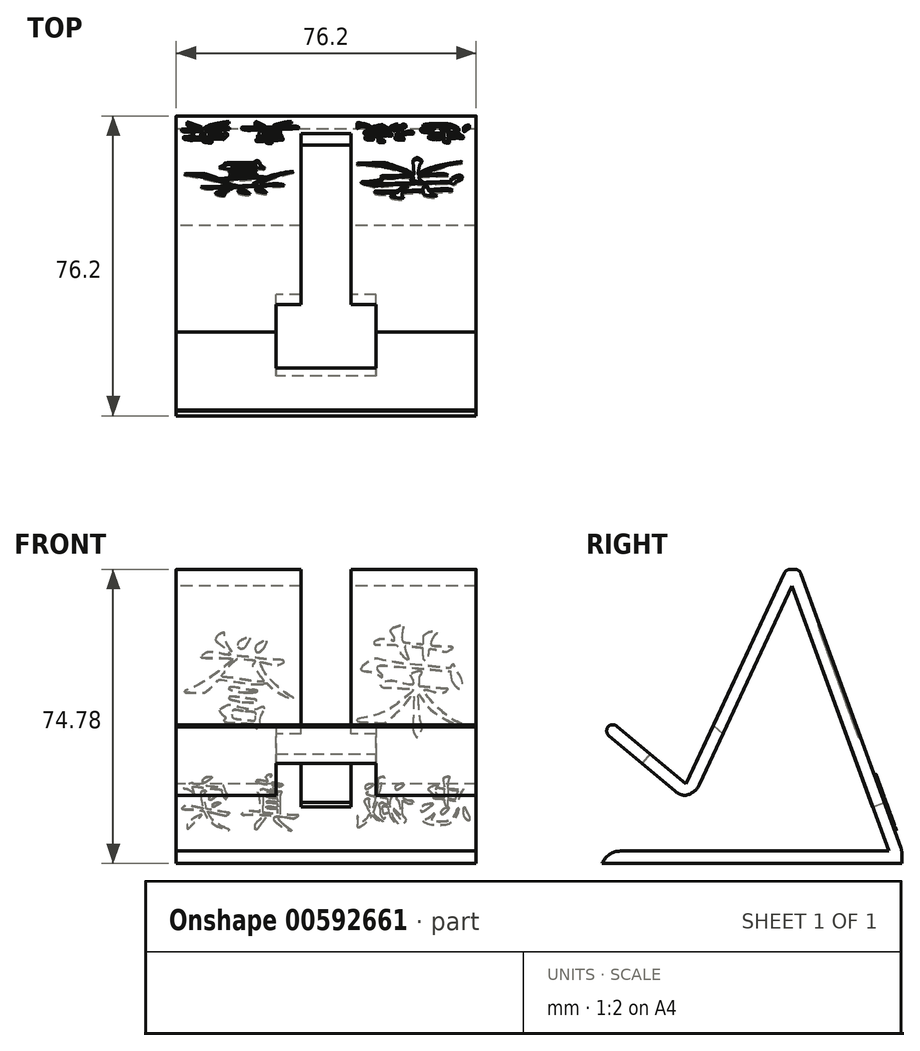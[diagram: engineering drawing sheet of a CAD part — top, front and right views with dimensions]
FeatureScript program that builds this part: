
annotation { "Feature Type Name" : "Feature", "Feature Type Description" : "" }
export const myFeature = defineFeature(function(context is Context, id is Id, definition is map)
    precondition{}
    {
        {
            var Q0;
            Q0=qCreatedBy(makeId("Top.planeOp"),FACE);
            var sketch = newSketch(context, id + "F0", { "sketchPlane" : qUnion([Q0])});
            skLineSegment(sketch, "E0.bottom", {"start": v(-50.93, 28.39) * mm, "end": v(25.27, 28.39) * mm});
            skLineSegment(sketch, "E0.top", {"start": v(-50.93, -47.81) * mm, "end": v(25.27, -47.81) * mm});
            skLineSegment(sketch, "E0.left", {"start": v(-50.93, 28.39) * mm, "end": v(-50.93, -47.81) * mm});
            skLineSegment(sketch, "E0.right", {"start": v(25.27, 28.39) * mm, "end": v(25.27, -47.81) * mm});
            skSolve(sketch);
        }
        {
            var Q0;
            Q0 = qSketchRegion(id + "F0", true);
            extrude(context, id + "F1", {"entities" : qUnion([Q0]), "depth" : 3.17 * mm, "offsetDistance" : 25.4 * mm});
        }
        {
            var Q0;
            Q0=makeQuery(id+"F1.opExtrude","SWEPT_FACE",FACE,{"disambiguationData":[OSD([sQuery(id+"F0.wireOp",EDGE,"E0.left")])]});
            var sketch = newSketch(context, id + "F2", { "sketchPlane" : qUnion([Q0])});
            skLineSegment(sketch, "E1", {"start": v(-28.39, 3.17) * mm, "end": v(-2.33, 74.78) * mm});
            skLineSegment(sketch, "E2", {"start": v(-25, 3.18) * mm, "end": v(1.05, 74.78) * mm});
            skLineSegment(sketch, "E3", {"start": v(1.05, 74.78) * mm, "end": v(-2.33, 74.78) * mm});
            skLineSegment(sketch, "E4", {"start": v(27.89, 17.23) * mm, "end": v(1.05, 74.78) * mm});
            skLineSegment(sketch, "E5", {"start": v(47.35, 33.56) * mm, "end": v(27.89, 17.23) * mm});
            skLineSegment(sketch, "E6", {"start": v(-0.48, 70.56) * mm, "end": v(24.39, 17.23) * mm});
            skLineSegment(sketch, "E7", {"start": v(24.39, 17.23) * mm, "end": v(27.89, 17.23) * mm});
            skLineSegment(sketch, "E8", {"start": v(47.35, 33.56) * mm, "end": v(45.3, 35.99) * mm});
            skLineSegment(sketch, "E9", {"start": v(45.3, 35.99) * mm, "end": v(26.5, 20.2) * mm});
            skSolve(sketch);
        }
        {
            var Q0;
            Q0 = qSketchRegion(id + "F2", true);
            var Q1;
            {var subQ6=sQuery(id+"F2.wireOp",EDGE,"E1");Q1=makeQuery(id+"F2.imprint","IMPRINT",FACE,{"disambiguationData":[TD([[makeQuery(id+"F2.imprint","IMPRINT",EDGE,{"derivedFrom":subQ6}),-1.0]])]});}
            extrude(context, id + "F3", {"entities" : qUnion([Q0, Q1]), "operationType" : NewBodyOperationType.ADD, "oppositeDirection" : true, "depth" : 76.2 * mm, "offsetDistance" : 25.4 * mm});
        }
        {
            var Q0;
            Q0=makeQuery(id+"F3.opExtrude","SWEPT_EDGE",EDGE,{"disambiguationData":[OSD([sQuery(id+"F2.wireOp",EDGE,"E2"),sQuery(id+"F2.wireOp",EDGE,"E3"),sQuery(id+"F2.wireOp",EDGE,"E4")])]});
            var Q1;
            Q1=makeQuery(id+"F3.opExtrude","SWEPT_EDGE",EDGE,{"disambiguationData":[OSD([sQuery(id+"F2.wireOp",EDGE,"E1"),sQuery(id+"F2.wireOp",EDGE,"E3")])]});
            fillet(context, id + "F4", {"entities" : qUnion([Q0, Q1]), "radius" : 1.71 * mm, "tangentPropagation" : true, "allowEdgeOverflow" : false});
        }
        {
            var Q0;
            {var subQ0=sQuery(id+"F0.wireOp",EDGE,"E0.bottom");Q0=makeQuery(id+"F3.boolean.opBoolean","MERGE",EDGE,{"derivedFrom":[makeQuery(id+"F1.opExtrude","CAP_EDGE",EDGE,{"disambiguationData":[OSD([subQ0])],"isStart":false}),makeQuery(id+"F3.opExtrude","SWEPT_EDGE",EDGE,{"disambiguationData":[OSD([subQ0,sQuery(id+"F0.wireOp",EDGE,"E0.left"),sQuery(id+"F2.wireOp",EDGE,"E1")])]})]});}
            fillet(context, id + "F5", {"entities" : qUnion([Q0]), "radius" : 5.08 * mm, "tangentPropagation" : true, "allowEdgeOverflow" : false});
        }
        {
            var Q0;
            Q0=makeQuery(id+"F3.opExtrude","SWEPT_EDGE",EDGE,{"disambiguationData":[OSD([sQuery(id+"F2.wireOp",EDGE,"E8"),sQuery(id+"F2.wireOp",EDGE,"E9")])]});
            var Q1;
            Q1=makeQuery(id+"F3.opExtrude","SWEPT_EDGE",EDGE,{"disambiguationData":[OSD([sQuery(id+"F2.wireOp",EDGE,"E5"),sQuery(id+"F2.wireOp",EDGE,"E8")])]});
            fillet(context, id + "F6", {"entities" : qUnion([Q0, Q1]), "radius" : 1.71 * mm, "tangentPropagation" : true, "allowEdgeOverflow" : false});
        }
        {
            var Q0;
            Q0=makeQuery(id+"F3.opExtrude","SWEPT_EDGE",EDGE,{"disambiguationData":[OSD([sQuery(id+"F2.wireOp",EDGE,"E6"),sQuery(id+"F2.wireOp",EDGE,"E7")])]});
            var Q1;
            Q1=makeQuery(id+"F3.opExtrude","SWEPT_EDGE",EDGE,{"disambiguationData":[OSD([sQuery(id+"F2.wireOp",EDGE,"E4"),sQuery(id+"F2.wireOp",EDGE,"E5"),sQuery(id+"F2.wireOp",EDGE,"E7")])]});
            fillet(context, id + "F7", {"entities" : qUnion([Q0, Q1]), "radius" : 5.08 * mm, "tangentPropagation" : true, "allowEdgeOverflow" : false});
        }
        {
            var Q0;
            Q0=makeQuery(id+"F1.opExtrude","CAP_EDGE",EDGE,{"disambiguationData":[OSD([sQuery(id+"F0.wireOp",EDGE,"E0.top")])],"isStart":false});
            fillet(context, id + "F8", {"entities" : qUnion([Q0]), "radius" : 5.08 * mm, "tangentPropagation" : true, "allowEdgeOverflow" : false});
        }
        {
            var Q0;
            Q0=makeQuery(id+"F3.opExtrude","SWEPT_FACE",FACE,{"disambiguationData":[OSD([sQuery(id+"F2.wireOp",EDGE,"E1")])]});
            var sketch = newSketch(context, id + "F9", { "sketchPlane" : qUnion([Q0])});
            skLineSegment(sketch, "E10.bottom", {"start": v(6.48, 6.38) * mm, "end": v(19.18, 6.38) * mm});
            skLineSegment(sketch, "E10.top", {"start": v(6.48, 82.58) * mm, "end": v(19.18, 82.58) * mm});
            skLineSegment(sketch, "E10.left", {"start": v(6.48, 6.38) * mm, "end": v(6.48, 82.58) * mm});
            skLineSegment(sketch, "E10.right", {"start": v(19.18, 6.38) * mm, "end": v(19.18, 82.58) * mm});
            skSolve(sketch);
        }
        {
            var Q0;
            Q0 = qSketchRegion(id + "F9", true);
            var Q1;
            Q1=makeQuery(id+"F3.opExtrude","SWEPT_FACE",FACE,{"disambiguationData":[OSD([sQuery(id+"F2.wireOp",EDGE,"E9")])]});
            extrude(context, id + "F10", {"entities" : qUnion([Q0]), "operationType" : NewBodyOperationType.REMOVE, "endBound" : BoundingType.UP_TO_SURFACE, "oppositeDirection" : true, "depth" : 38.1 * mm, "endBoundEntityFace" : qUnion([Q1]), "offsetDistance" : 25.4 * mm});
        }
        {
            var Q0;
            Q0=makeQuery(id+"F3.opExtrude","SWEPT_FACE",FACE,{"disambiguationData":[OSD([sQuery(id+"F2.wireOp",EDGE,"E5")])]});
            var sketch = newSketch(context, id + "F11", { "sketchPlane" : qUnion([Q0])});
            skLineSegment(sketch, "E11.bottom", {"start": v(-0.13, 45.2) * mm, "end": v(-25.53, 45.2) * mm});
            skLineSegment(sketch, "E11.top", {"start": v(-0.13, 25.32) * mm, "end": v(-25.53, 25.32) * mm});
            skLineSegment(sketch, "E11.left", {"start": v(-0.13, 45.2) * mm, "end": v(-0.13, 25.32) * mm});
            skLineSegment(sketch, "E11.right", {"start": v(-25.53, 45.2) * mm, "end": v(-25.53, 25.32) * mm});
            skSolve(sketch);
        }
        {
            var Q0;
            Q0 = qSketchRegion(id + "F11", true);
            extrude(context, id + "F12", {"entities" : qUnion([Q0]), "operationType" : NewBodyOperationType.REMOVE, "oppositeDirection" : true, "depth" : 19.05 * mm, "offsetDistance" : 25.4 * mm});
        }
        {
            var Q0;
            Q0=makeQuery(id+"F3.opExtrude","SWEPT_FACE",FACE,{"disambiguationData":[OSD([sQuery(id+"F2.wireOp",EDGE,"E1")])]});
            var sketch = newSketch(context, id + "F13", { "sketchPlane" : qUnion([Q0])});
            skFitSpline(sketch, "E12", {"points": [v(-12.22, 36.96) * mm, v(-14.1, 36.55) * mm, v(-16.43, 36.17) * mm, v(-17.56, 36.53) * mm, v(-18.06, 37.15) * mm, v(-17.5, 37.27) * mm, v(-14.44, 37.5) * mm, v(-11.43, 37.83) * mm, v(-10.85, 38.05) * mm, v(-10.88, 39.14) * mm, v(-11.1, 40.96) * mm, v(-11.58, 41.5) * mm, v(-11.2, 41.95) * mm, v(-10.09, 41.85) * mm, v(-8.74, 41.2) * mm, v(-8.7, 40.6) * mm, v(-9.04, 39.97) * mm, v(-9.27, 39.23) * mm, v(-9.22, 38.43) * mm, v(-8.6, 38.33) * mm, v(-6.3, 38.8) * mm, v(-4.43, 39.3) * mm, v(-3.5, 39.37) * mm, v(-1.9, 39.1) * mm, v(-1.1, 38.55) * mm, v(-1.05, 38.03) * mm, v(-1.68, 37.61) * mm, v(-3.4, 37.56) * mm, v(-5.42, 37.47) * mm, v(-7.94, 37.28) * mm, v(-9.11, 37.23) * mm, v(-9.14, 36.74) * mm, v(-6.85, 34.65) * mm, v(-4.68, 32.8) * mm, v(-2.27, 31.23) * mm, v(0.99, 29.95) * mm, v(3.33, 29.43) * mm, v(4.76, 29.07) * mm, v(5, 28.78) * mm, v(4.7, 28.44) * mm, v(2.36, 28.14) * mm, v(-2.03, 28.02) * mm, v(-2.32, 28.17) * mm, v(-3.27, 28.96) * mm, v(-5.28, 30.98) * mm, v(-7.8, 33.82) * mm, v(-9.14, 35.74) * mm, v(-9.34, 35.78) * mm, v(-9.45, 35.4) * mm, v(-9.37, 32.66) * mm, v(-9.28, 28.6) * mm, v(-9.25, 26.13) * mm, v(-9.59, 25.05) * mm, v(-10.07, 24.3) * mm, v(-10.36, 24.21) * mm, v(-10.6, 24.45) * mm, v(-11.18, 25.54) * mm, v(-11.54, 26.68) * mm, v(-11.44, 27.54) * mm, v(-11.12, 28.58) * mm, v(-10.83, 31.04) * mm, v(-10.62, 34.03) * mm, v(-10.65, 35.63) * mm, v(-10.83, 35.72) * mm, v(-10.96, 35.5) * mm, v(-13.08, 32.37) * mm, v(-15.67, 30.1) * mm, v(-17.98, 28.68) * mm, v(-20.8, 27.47) * mm, v(-21.64, 27.4) * mm, v(-21.73, 27.63) * mm, v(-21.34, 27.9) * mm, v(-19.9, 28.62) * mm, v(-17.22, 30.6) * mm, v(-15.3, 32.34) * mm, v(-13.41, 34.54) * mm, v(-12.47, 35.9) * mm, v(-12.22, 36.96) * mm]});
            skFitSpline(sketch, "E13", {"points": [v(-19.06, 39.57) * mm, v(-19.6, 38.51) * mm, v(-20.44, 37.57) * mm, v(-21.16, 37.34) * mm, v(-21.67, 38.04) * mm, v(-21.86, 38.9) * mm, v(-21.65, 39.92) * mm, v(-20.9, 41.2) * mm, v(-20.15, 42.27) * mm, v(-19.89, 43.27) * mm, v(-19.76, 43.82) * mm, v(-19.4, 43.9) * mm, v(-19.05, 43.55) * mm, v(-18.71, 42.98) * mm, v(-17.94, 42.87) * mm, v(-14.98, 43.18) * mm, v(-11.95, 43.58) * mm, v(-9.74, 43.77) * mm, v(-7.28, 44.03) * mm, v(-5.47, 44.28) * mm, v(-2.65, 44.78) * mm, v(-1.11, 45.14) * mm, v(0, 45.43) * mm, v(0.84, 45.26) * mm, v(1.7, 44.76) * mm, v(2.84, 44.02) * mm, v(3.67, 43.25) * mm, v(4, 42.73) * mm, v(3.82, 42.28) * mm, v(2.66, 41.97) * mm, v(1.78, 41.89) * mm, v(0.9, 41.61) * mm, v(-0.12, 41.14) * mm, v(-0.93, 40.62) * mm, v(-1.3, 40.46) * mm, v(-1.53, 40.78) * mm, v(-0.9, 41.54) * mm, v(-0.27, 42.4) * mm, v(-0.2, 43.08) * mm, v(-0.62, 43.52) * mm, v(-4.26, 43.32) * mm, v(-6.92, 43.12) * mm, v(-9.53, 42.88) * mm, v(-11.66, 42.69) * mm, v(-14.8, 42.39) * mm, v(-17.35, 42.11) * mm, v(-18.49, 42.05) * mm, v(-18.69, 42) * mm, v(-18.74, 41.55) * mm, v(-19.06, 39.57) * mm]});
            skFitSpline(sketch, "E14", {"points": [v(-14.66, 47.79) * mm, v(-13.72, 47.93) * mm, v(-13.25, 47.66) * mm, v(-13.1, 46.6) * mm, v(-12.96, 45.72) * mm, v(-12.6, 44.94) * mm, v(-12.33, 44.79) * mm, v(-11.95, 45.2) * mm, v(-11.84, 46.2) * mm, v(-11.81, 47.1) * mm, v(-11.79, 47.77) * mm, v(-11.74, 48.14) * mm, v(-11.21, 48.3) * mm, v(-9.9, 48.47) * mm, v(-8.27, 48.64) * mm, v(-7.27, 48.68) * mm, v(-7.15, 48.49) * mm, v(-7.37, 47.49) * mm, v(-7.75, 46.34) * mm, v(-8.05, 45.5) * mm, v(-8.02, 45.09) * mm, v(-7.69, 45.08) * mm, v(-7, 45.7) * mm, v(-6.37, 46.65) * mm, v(-5.65, 48.03) * mm, v(-5.33, 48.8) * mm, v(-4.77, 49.02) * mm, v(-3.86, 49.06) * mm, v(-2.26, 49.07) * mm, v(-0.5, 49.07) * mm, v(0.34, 49.1) * mm, v(0.52, 49.39) * mm, v(0.5, 49.95) * mm, v(-0.02, 50.39) * mm, v(-0.81, 50.75) * mm, v(-1.97, 50.8) * mm, v(-2.82, 50.7) * mm, v(-3.86, 50.43) * mm, v(-4.4, 50.28) * mm, v(-4.55, 50.81) * mm, v(-4.02, 51.86) * mm, v(-3.55, 52.9) * mm, v(-3.85, 53.54) * mm, v(-4.53, 53.9) * mm, v(-5.21, 54.14) * mm, v(-6.14, 54.45) * mm, v(-6.73, 54.28) * mm, v(-6.77, 53.77) * mm, v(-6.63, 53.31) * mm, v(-6.5, 52.18) * mm, v(-6.47, 50.8) * mm, v(-6.73, 50) * mm, v(-7.75, 49.7) * mm, v(-9.53, 49.51) * mm, v(-10.88, 49.4) * mm, v(-11.64, 49.35) * mm, v(-11.88, 49.56) * mm, v(-11.93, 50.52) * mm, v(-11.92, 51.54) * mm, v(-12.15, 51.84) * mm, v(-13.05, 52.47) * mm, v(-14.01, 52.78) * mm, v(-15.11, 52.8) * mm, v(-15.3, 52.5) * mm, v(-15.29, 52.24) * mm, v(-14.8, 51.78) * mm, v(-14.45, 51.35) * mm, v(-14.06, 50.48) * mm, v(-13.77, 49.33) * mm, v(-14.07, 48.96) * mm, v(-15.48, 48.84) * mm, v(-17.37, 48.77) * mm, v(-18.94, 48.68) * mm, v(-19.25, 48.48) * mm, v(-19.2, 48.12) * mm, v(-18.67, 47.68) * mm, v(-17.8, 47.2) * mm, v(-17.14, 47.17) * mm, v(-16.42, 47.36) * mm, v(-15.6, 47.62) * mm, v(-14.66, 47.79) * mm]});
            skFitSpline(sketch, "E15", {"points": [v(28.87, 38.54) * mm, v(28.32, 38.79) * mm, v(27.78, 38.62) * mm, v(26.46, 37.32) * mm, v(24.68, 36.02) * mm, v(22.98, 35.12) * mm, v(22, 34.76) * mm, v(21.31, 34.52) * mm, v(21.13, 34.7) * mm, v(21.63, 35.1) * mm, v(23.1, 36.12) * mm, v(24.87, 37.53) * mm, v(26.57, 39.28) * mm, v(27.87, 40.84) * mm, v(28.96, 42.7) * mm, v(29.36, 43.66) * mm, v(29.57, 44.34) * mm, v(29.4, 44.43) * mm, v(27.84, 44.14) * mm, v(25.92, 43.63) * mm, v(25.16, 43.68) * mm, v(23.74, 44.29) * mm, v(23.54, 44.59) * mm, v(23.75, 44.93) * mm, v(25.94, 45.16) * mm, v(28.85, 45.34) * mm, v(30.94, 45.7) * mm, v(33.66, 45.93) * mm, v(34.73, 46.04) * mm, v(35.61, 46.19) * mm, v(36.32, 46.77) * mm, v(37.07, 47.78) * mm, v(37.96, 49.23) * mm, v(38.45, 50.58) * mm, v(38.66, 51.6) * mm, v(38.64, 52.3) * mm, v(38.78, 52.36) * mm, v(39.36, 52.32) * mm, v(40.3, 51.7) * mm, v(40.84, 50.98) * mm, v(40.9, 50.38) * mm, v(40.53, 49.87) * mm, v(39.45, 49.03) * mm, v(38.35, 47.98) * mm, v(37.82, 47.38) * mm, v(37.17, 46.67) * mm, v(37.23, 46.43) * mm, v(38.42, 46.5) * mm, v(40.07, 46.9) * mm, v(42, 47.13) * mm, v(43.14, 47.06) * mm, v(43.92, 46.55) * mm, v(44.53, 45.94) * mm, v(44.5, 45.75) * mm, v(43.24, 45.61) * mm, v(39.94, 45.6) * mm, v(36.74, 45.41) * mm, v(36.58, 45.35) * mm, v(36.68, 45.08) * mm, v(38.62, 43.29) * mm, v(40.68, 41.52) * mm, v(42.75, 39.98) * mm, v(44.15, 39.06) * mm, v(46.8, 37.57) * mm, v(48.48, 36.84) * mm, v(48.78, 36.66) * mm, v(48.79, 36.37) * mm, v(47.08, 36.29) * mm, v(43.85, 36.19) * mm, v(42.94, 36.81) * mm, v(41.03, 38.67) * mm, v(40.29, 39.6) * mm, v(39.83, 39.74) * mm, v(38.7, 39.55) * mm, v(37.17, 39.3) * mm, v(34.5, 38.96) * mm, v(31.57, 38.49) * mm, v(29.78, 38.52) * mm, v(28.87, 38.54) * mm]});
            skFitSpline(sketch, "E16", {"points": [v(29.58, 39.3) * mm, v(28.85, 39.3) * mm, v(28.63, 39.35) * mm, v(28.81, 39.71) * mm, v(29.58, 40.78) * mm, v(30.26, 41.84) * mm, v(30.75, 42.58) * mm, v(31.36, 43.35) * mm, v(31.34, 43.82) * mm, v(31.1, 44.18) * mm, v(30.84, 44.55) * mm, v(30.9, 44.77) * mm, v(31.34, 44.91) * mm, v(32.5, 44.97) * mm, v(34.1, 45.18) * mm, v(35.51, 45.2) * mm, v(35.96, 44.84) * mm, v(37.1, 43.83) * mm, v(38.28, 42.34) * mm, v(39.34, 40.87) * mm, v(39.26, 40.62) * mm, v(37.65, 40.45) * mm, v(34.23, 39.9) * mm, v(32, 39.54) * mm, v(29.58, 39.3) * mm]});
            skFitSpline(sketch, "E17", {"points": [v(33.37, 41.57) * mm, v(34.26, 40.87) * mm, v(34.66, 40.77) * mm, v(35.15, 41.13) * mm, v(35.25, 41.82) * mm, v(34.6, 42.5) * mm, v(33.78, 42.7) * mm, v(32.89, 42.69) * mm, v(32.67, 42.52) * mm, v(32.76, 42.17) * mm, v(33.37, 41.57) * mm]});
            skFitSpline(sketch, "E18", {"points": [v(32.51, 27.86) * mm, v(31.51, 27.8) * mm, v(31.07, 27.56) * mm, v(30.8, 26.82) * mm, v(30.58, 26.52) * mm, v(30.1, 26.66) * mm, v(29.7, 28.18) * mm, v(29.21, 30.3) * mm, v(28.7, 31.25) * mm, v(28.5, 31.59) * mm, v(28.58, 32.3) * mm, v(29.3, 32.26) * mm, v(30.4, 31.78) * mm, v(31.25, 31.52) * mm, v(32.77, 31.73) * mm, v(34.74, 32.2) * mm, v(36.37, 32.66) * mm, v(37.15, 32.81) * mm, v(38.42, 32.54) * mm, v(39.56, 31.8) * mm, v(39.91, 31.43) * mm, v(39.6, 30.72) * mm, v(38.8, 29.92) * mm, v(38.44, 29.53) * mm, v(38.47, 29.1) * mm, v(38.67, 28.93) * mm, v(38.6, 28.34) * mm, v(37.6, 28.12) * mm, v(35.2, 27.98) * mm, v(32.51, 27.86) * mm]});
            skFitSpline(sketch, "E19", {"points": [v(33.8, 31.2) * mm, v(35.08, 31.41) * mm, v(36.14, 31.54) * mm, v(36.57, 31.3) * mm, v(36.78, 30.48) * mm, v(36.68, 29.61) * mm, v(36.14, 29.21) * mm, v(34.3, 28.97) * mm, v(32.33, 28.73) * mm, v(31.52, 28.6) * mm, v(30.98, 28.7) * mm, v(30.77, 29.51) * mm, v(30.74, 30.65) * mm, v(31.4, 30.98) * mm, v(33.8, 31.2) * mm]});
            skFitSpline(sketch, "E20", {"points": [v(34.26, 33.66) * mm, v(31.84, 33.59) * mm, v(30.84, 33.62) * mm, v(30.5, 33.82) * mm, v(30.62, 34.2) * mm, v(32.34, 34.57) * mm, v(34.51, 34.92) * mm, v(36.28, 35.11) * mm, v(37.31, 35.06) * mm, v(37.48, 34.64) * mm, v(37.03, 34.35) * mm, v(34.92, 33.82) * mm, v(34.26, 33.66) * mm]});
            skFitSpline(sketch, "E21", {"points": [v(32.07, 36.13) * mm, v(34.45, 36.23) * mm, v(36.9, 36.8) * mm, v(37.44, 37.17) * mm, v(37.38, 37.56) * mm, v(37, 37.83) * mm, v(35.13, 37.6) * mm, v(33.32, 37.2) * mm, v(31.96, 37.04) * mm, v(30.8, 37.05) * mm, v(30.33, 36.71) * mm, v(30.53, 36.37) * mm, v(32.07, 36.13) * mm]});
            skFitSpline(sketch, "E22", {"points": [v(28.89, 48) * mm, v(29.5, 47.33) * mm, v(30.07, 47) * mm, v(30.51, 47.2) * mm, v(30.7, 48.43) * mm, v(30.2, 49.36) * mm, v(29.2, 49.94) * mm, v(28.41, 50.38) * mm, v(28.01, 50.2) * mm, v(28.14, 49.48) * mm, v(28.63, 48.37) * mm, v(28.89, 48) * mm]});
            skFitSpline(sketch, "E23", {"points": [v(32.93, 49.4) * mm, v(33.47, 48.48) * mm, v(34.27, 48) * mm, v(34.9, 48.23) * mm, v(35.23, 48.88) * mm, v(35.11, 49.73) * mm, v(34.38, 50.45) * mm, v(33.45, 50.91) * mm, v(32.48, 51.16) * mm, v(32.19, 51) * mm, v(32.3, 50.55) * mm, v(32.93, 49.4) * mm]});
            skSolve(sketch);
        }
        {
            var Q0;
            Q0 = qSketchRegion(id + "F13", true);
            extrude(context, id + "F14", {"entities" : qUnion([Q0]), "operationType" : NewBodyOperationType.REMOVE, "oppositeDirection" : true, "depth" : 0.5 * mm, "offsetDistance" : 25.4 * mm});
        }
        {
            var Q0;
            {var subQ8=sQuery(id+"F2.wireOp",EDGE,"E1");var subQ9=sQuery(id+"F0.wireOp",EDGE,"E0.left");Q0=makeQuery(id+"F14.boolean.opBoolean","SPLIT",FACE,{"disambiguationData":[TD([makeQuery(id+"F1.opExtrude","SWEPT_FACE",FACE,{"disambiguationData":[OSD([subQ9])]})])],"derivedFrom":makeQuery(id+"F3.opExtrude","SWEPT_FACE",FACE,{"disambiguationData":[OSD([subQ8])]})});}
            var sketch = newSketch(context, id + "F15", { "sketchPlane" : qUnion([Q0])});
            skPoint(sketch, "E24.secondSnap0", {"position": v(-9.78, -1.72) * mm});
            skFitSpline(sketch, "E25", {"points": [v(-18.07, 11) * mm, v(-18.1, 10.25) * mm, v(-19.22, 10.07) * mm, v(-20.6, 9.88) * mm, v(-21.04, 10.01) * mm, v(-21.53, 10.1) * mm, v(-21.94, 10.05) * mm, v(-22, 9.9) * mm, v(-21.66, 9.4) * mm, v(-21.18, 8.46) * mm, v(-20.9, 7.48) * mm, v(-20.67, 6.76) * mm, v(-20.46, 6.26) * mm, v(-20.29, 6.15) * mm, v(-20.14, 6.27) * mm, v(-20.06, 6.55) * mm, v(-19.84, 6.74) * mm, v(-19.16, 6.78) * mm, v(-18.64, 6.91) * mm, v(-18.25, 7) * mm, v(-18.06, 7) * mm, v(-18.03, 6.38) * mm, v(-18.02, 5.55) * mm, v(-17.92, 5.24) * mm, v(-17.83, 5.18) * mm, v(-17.54, 5.64) * mm, v(-17.3, 6.4) * mm, v(-17.22, 6.89) * mm, v(-17.2, 7.1) * mm, v(-16.8, 7.18) * mm, v(-16.02, 7.24) * mm, v(-15.31, 7.29) * mm, v(-14.63, 7.4) * mm, v(-14.47, 7.55) * mm, v(-14.55, 7.83) * mm, v(-14.69, 7.96) * mm, v(-14.48, 8.34) * mm, v(-13.87, 9.02) * mm, v(-13.36, 9.54) * mm, v(-13.13, 9.87) * mm, v(-13.17, 10.08) * mm, v(-13.9, 10.6) * mm, v(-14.65, 11) * mm, v(-15.27, 11.05) * mm, v(-16.49, 10.63) * mm, v(-17.03, 10.45) * mm, v(-17.17, 10.48) * mm, v(-17.19, 11) * mm, v(-17.12, 11.83) * mm, v(-16.96, 12.54) * mm, v(-17.06, 12.93) * mm, v(-17.49, 13.24) * mm, v(-18.18, 13.4) * mm, v(-18.42, 13.35) * mm, v(-18.5, 13.15) * mm, v(-18.38, 12.8) * mm, v(-18.16, 11.83) * mm, v(-18.07, 11) * mm]});
            skFitSpline(sketch, "E26", {"points": [v(-20.44, 8.6) * mm, v(-20.6, 9.01) * mm, v(-20.57, 9.41) * mm, v(-19.94, 9.51) * mm, v(-19, 9.7) * mm, v(-18.15, 9.77) * mm, v(-18.08, 9.3) * mm, v(-18.07, 7.5) * mm, v(-18.1, 7.4) * mm, v(-18.74, 7.32) * mm, v(-19.58, 7.17) * mm, v(-19.96, 7.14) * mm, v(-20.1, 7.4) * mm, v(-20.34, 8.3) * mm, v(-20.44, 8.6) * mm]});
            skFitSpline(sketch, "E27", {"points": [v(-17.16, 8.14) * mm, v(-17.15, 7.74) * mm, v(-17.03, 7.67) * mm, v(-16.47, 7.75) * mm, v(-15.8, 7.9) * mm, v(-15.48, 8.07) * mm, v(-15.23, 8.65) * mm, v(-15.09, 9.27) * mm, v(-15.06, 10.03) * mm, v(-15.2, 10.28) * mm, v(-15.7, 10.3) * mm, v(-16.43, 10.19) * mm, v(-17.14, 10.05) * mm, v(-17.17, 9.9) * mm, v(-17.15, 8.72) * mm, v(-17.16, 8.14) * mm]});
            skFitSpline(sketch, "E28", {"points": [v(-22.67, 4.33) * mm, v(-23.04, 3.53) * mm, v(-23.5, 2.65) * mm, v(-23.56, 2.32) * mm, v(-23.56, 1.63) * mm, v(-23.38, 1.45) * mm, v(-22.9, 1.7) * mm, v(-22.4, 2.29) * mm, v(-22.13, 2.95) * mm, v(-22.02, 4.05) * mm, v(-22.13, 4.87) * mm, v(-22.24, 5.08) * mm, v(-22.43, 5.06) * mm, v(-22.48, 4.8) * mm, v(-22.67, 4.33) * mm]});
            skFitSpline(sketch, "E29", {"points": [v(-20.85, 4.17) * mm, v(-20.88, 4.63) * mm, v(-20.8, 4.8) * mm, v(-20.65, 4.74) * mm, v(-20.3, 4.34) * mm, v(-20.16, 3.95) * mm, v(-19.8, 2.97) * mm, v(-19.02, 1.92) * mm, v(-18.07, 1.33) * mm, v(-16.79, 1.12) * mm, v(-15.4, 1.13) * mm, v(-14.37, 1.37) * mm, v(-14.04, 1.51) * mm, v(-14.03, 1.72) * mm, v(-14.41, 2.48) * mm, v(-14.7, 3) * mm, v(-14.68, 3.24) * mm, v(-14.56, 3.29) * mm, v(-14.22, 3) * mm, v(-13.5, 2.34) * mm, v(-12.6, 1.8) * mm, v(-12.08, 1.6) * mm, v(-11.88, 1.45) * mm, v(-11.82, 1.22) * mm, v(-12.7, 0.73) * mm, v(-14.25, 0.34) * mm, v(-16.02, 0.3) * mm, v(-17.87, 0.41) * mm, v(-18.72, 0.8) * mm, v(-19.4, 1.28) * mm, v(-20.16, 2.22) * mm, v(-20.59, 3.2) * mm, v(-20.85, 4.17) * mm]});
            skFitSpline(sketch, "E30", {"points": [v(-17.97, 4.16) * mm, v(-18.34, 4.6) * mm, v(-18.38, 4.92) * mm, v(-18.16, 5) * mm, v(-17.51, 4.8) * mm, v(-16.74, 4.34) * mm, v(-16.32, 3.85) * mm, v(-16.28, 3.44) * mm, v(-16.66, 3.17) * mm, v(-17.16, 3.4) * mm, v(-17.72, 3.9) * mm, v(-17.97, 4.16) * mm]});
            skFitSpline(sketch, "E31", {"points": [v(-13.65, 5.23) * mm, v(-14.19, 5.67) * mm, v(-14.34, 5.8) * mm, v(-14.3, 5.97) * mm, v(-13.67, 5.97) * mm, v(-12.57, 5.8) * mm, v(-11.89, 5.53) * mm, v(-11.35, 5) * mm, v(-11.22, 4.63) * mm, v(-11.21, 4.09) * mm, v(-11.32, 3.9) * mm, v(-11.75, 3.93) * mm, v(-12.41, 4.28) * mm, v(-13.12, 4.8) * mm, v(-13.65, 5.23) * mm]});
            skFitSpline(sketch, "E32", {"points": [v(-6.53, 5.34) * mm, v(-6.54, 6.6) * mm, v(-6.57, 6.8) * mm, v(-6.72, 6.8) * mm, v(-7.17, 6.53) * mm, v(-7.91, 6.1) * mm, v(-8.17, 6) * mm, v(-8.7, 6) * mm, v(-9.18, 6.22) * mm, v(-9.33, 6.4) * mm, v(-9.29, 6.63) * mm, v(-8.98, 6.76) * mm, v(-8.43, 6.77) * mm, v(-7.81, 6.95) * mm, v(-7.09, 7.29) * mm, v(-6.55, 7.8) * mm, v(-6.35, 7.99) * mm, v(-5.82, 8) * mm, v(-5.36, 7.86) * mm, v(-5.06, 7.7) * mm, v(-4.93, 7.52) * mm, v(-5.04, 7.29) * mm, v(-5.43, 6.91) * mm, v(-5.65, 6.38) * mm, v(-5.85, 5.38) * mm, v(-5.97, 3.27) * mm, v(-5.95, 3.03) * mm, v(-5.9, 2.99) * mm, v(-5.75, 3.16) * mm, v(-5.15, 3.82) * mm, v(-4.64, 4.31) * mm, v(-4.42, 4.5) * mm, v(-4.27, 4.55) * mm, v(-4.23, 4.43) * mm, v(-4.36, 4.05) * mm, v(-5.23, 2.9) * mm, v(-5.91, 2) * mm, v(-6.64, 0.83) * mm, v(-6.8, 0.68) * mm, v(-7.03, 0.75) * mm, v(-7.34, 1.2) * mm, v(-7.44, 1.48) * mm, v(-7.45, 1.84) * mm, v(-7.22, 2.14) * mm, v(-6.8, 2.66) * mm, v(-6.6, 3.3) * mm, v(-6.53, 4.7) * mm, v(-6.53, 5.34) * mm]});
            skFitSpline(sketch, "E33", {"points": [v(-3.07, 3.82) * mm, v(-3.58, 2.35) * mm, v(-4.52, 1.12) * mm, v(-5.2, 0.6) * mm, v(-5.38, 0.62) * mm, v(-5.34, 0.75) * mm, v(-4.97, 1.22) * mm, v(-4.48, 1.94) * mm, v(-4.07, 2.86) * mm, v(-3.75, 3.96) * mm, v(-3.5, 5.1) * mm, v(-3.43, 6.49) * mm, v(-3.64, 7.29) * mm, v(-3.93, 7.93) * mm, v(-3.9, 8.24) * mm, v(-3.7, 8.37) * mm, v(-3.28, 8.25) * mm, v(-2.76, 8.08) * mm, v(-2.33, 8.14) * mm, v(-1.07, 8.38) * mm, v(-0.67, 8.54) * mm, v(-0.63, 8.62) * mm, v(-0.88, 9.46) * mm, v(-1.2, 10.9) * mm, v(-1.35, 12.01) * mm, v(-1.56, 12.33) * mm, v(-1.9, 12.67) * mm, v(-2, 12.92) * mm, v(-1.9, 13.19) * mm, v(-1.58, 13.23) * mm, v(-1.12, 13.18) * mm, v(-0.8, 13.04) * mm, v(-0.34, 12.78) * mm, v(-0.31, 12.55) * mm, v(-0.37, 11.28) * mm, v(-0.26, 10.06) * mm, v(-0.02, 8.8) * mm, v(0.08, 8.72) * mm, v(0.57, 8.82) * mm, v(1.26, 9.05) * mm, v(1.87, 9.13) * mm, v(2.36, 9.09) * mm, v(2.6, 8.95) * mm, v(2.67, 8.8) * mm, v(2.51, 8.63) * mm, v(1.97, 8.41) * mm, v(1, 8.14) * mm, v(0.26, 8.09) * mm, v(0.23, 8.01) * mm, v(0.45, 6.9) * mm, v(0.87, 5.37) * mm, v(1.15, 4.46) * mm, v(1.29, 4.23) * mm, v(1.4, 4.23) * mm, v(1.5, 4.57) * mm, v(1.82, 5.52) * mm, v(1.9, 6.87) * mm, v(1.88, 7.29) * mm, v(2.23, 7.35) * mm, v(2.76, 7.16) * mm, v(3.14, 6.77) * mm, v(3.17, 6.6) * mm, v(3.09, 6.25) * mm, v(2.83, 5.87) * mm, v(2.52, 5.22) * mm, v(2.1, 4.3) * mm, v(1.7, 3.66) * mm, v(1.69, 3.44) * mm, v(2.63, 1.98) * mm, v(3.38, 1.3) * mm, v(3.73, 1.1) * mm, v(3.85, 1.1) * mm, v(4.04, 1.37) * mm, v(4.59, 2.23) * mm, v(4.86, 2.67) * mm, v(4.95, 2.66) * mm, v(4.95, 2.13) * mm, v(4.85, 1.14) * mm, v(4.94, 0.24) * mm, v(5, -0.1) * mm, v(4.82, -0.33) * mm, v(4.24, -0.23) * mm, v(3.24, 0.44) * mm, v(2.13, 1.5) * mm, v(1.45, 2.46) * mm, v(1.27, 2.8) * mm, v(1.23, 2.88) * mm, v(1.07, 2.81) * mm, v(0.54, 2.27) * mm, v(-0.33, 1.62) * mm, v(-1.26, 1.2) * mm, v(-1.52, 1.12) * mm, v(-1.62, 1.18) * mm, v(-1.44, 1.3) * mm, v(-0.74, 1.85) * mm, v(0.3, 2.82) * mm, v(0.72, 3.34) * mm, v(0.84, 3.58) * mm, v(0.72, 3.97) * mm, v(0.24, 5.25) * mm, v(-0.11, 6.38) * mm, v(-0.44, 7.62) * mm, v(-0.5, 7.87) * mm, v(-0.66, 7.9) * mm, v(-1.49, 7.71) * mm, v(-2.52, 7.52) * mm, v(-2.7, 7.37) * mm, v(-2.74, 6.3) * mm, v(-2.75, 5.88) * mm, v(-2.68, 5.8) * mm, v(-2.4, 5.8) * mm, v(-1.81, 6.12) * mm, v(-1.34, 6.24) * mm, v(-0.9, 6.06) * mm, v(-0.52, 5.7) * mm, v(-0.64, 5.34) * mm, v(-0.78, 4.95) * mm, v(-0.8, 4.05) * mm, v(-0.94, 3.17) * mm, v(-1.4, 2.28) * mm, v(-1.86, 2) * mm, v(-2.04, 2.02) * mm, v(-2.2, 2.27) * mm, v(-2.44, 2.84) * mm, v(-2.67, 3.13) * mm, v(-2.78, 3.25) * mm, v(-2.72, 3.38) * mm, v(-2.32, 3.32) * mm, v(-2.14, 3.24) * mm, v(-1.84, 3.28) * mm, v(-1.56, 4.23) * mm, v(-1.54, 5.2) * mm, v(-1.64, 5.39) * mm, v(-1.95, 5.4) * mm, v(-2.7, 5.2) * mm, v(-2.85, 5.16) * mm, v(-2.9, 4.8) * mm, v(-3.07, 3.82) * mm]});
            skFitSpline(sketch, "E34", {"points": [v(1.02, 10.91) * mm, v(0.8, 11.07) * mm, v(0.81, 11.26) * mm, v(1.19, 11.33) * mm, v(2.08, 11.26) * mm, v(2.6, 11.01) * mm, v(2.87, 10.74) * mm, v(2.91, 10.32) * mm, v(2.83, 10.07) * mm, v(2.48, 10.03) * mm, v(2.04, 10.2) * mm, v(1.46, 10.56) * mm, v(1.02, 10.91) * mm]});
            skFitSpline(sketch, "E35", {"points": [v(-6.36, 10.51) * mm, v(-6.96, 11.07) * mm, v(-7, 11.25) * mm, v(-6.78, 11.35) * mm, v(-5.81, 11.3) * mm, v(-5.13, 10.98) * mm, v(-4.73, 10.6) * mm, v(-4.7, 10.14) * mm, v(-4.9, 9.85) * mm, v(-5.2, 9.8) * mm, v(-5.68, 10) * mm, v(-6.21, 10.41) * mm, v(-6.36, 10.51) * mm]});
            skFitSpline(sketch, "E36", {"points": [v(22.2, 2.2) * mm, v(21.23, 2.05) * mm, v(20.78, 2.12) * mm, v(20.2, 2.48) * mm, v(19.83, 2.78) * mm, v(19.8, 2.84) * mm, v(20.12, 2.87) * mm, v(21.6, 2.9) * mm, v(23.3, 3.05) * mm, v(24.24, 3.19) * mm, v(24.43, 3.25) * mm, v(24.45, 3.33) * mm, v(24.43, 4.67) * mm, v(24.43, 6.25) * mm, v(24.4, 7.76) * mm, v(24.34, 8.47) * mm, v(24.14, 8.99) * mm, v(24.08, 9.14) * mm, v(24.14, 9.27) * mm, v(24.42, 9.28) * mm, v(24.73, 9.22) * mm, v(25.26, 9.2) * mm, v(25.95, 9.26) * mm, v(26.07, 9.35) * mm, v(26.2, 9.82) * mm, v(26.46, 10.84) * mm, v(26.42, 10.94) * mm, v(25.85, 10.85) * mm, v(24.9, 10.7) * mm, v(24.36, 10.75) * mm, v(23.8, 11.05) * mm], "startDerivative": vector(-24.24, -4.56) * mm, "endDerivative": vector(-16, 9.95) * mm});
            skFitSpline(sketch, "E37", {"points": [v(23.8, 11.05) * mm, v(23.8, 11.17) * mm, v(23.92, 11.19) * mm, v(24.46, 11.3) * mm, v(25.13, 11.43) * mm, v(26.26, 11.67) * mm, v(26.63, 11.77) * mm, v(26.74, 12.09) * mm, v(26.83, 12.57) * mm, v(26.92, 13.2) * mm, v(26.89, 13.35) * mm, v(26.7, 13.53) * mm, v(26.63, 13.65) * mm, v(26.78, 13.87) * mm, v(27.37, 13.81) * mm, v(27.91, 13.55) * mm, v(28.16, 13.22) * mm, v(28.1, 12.88) * mm, v(27.91, 12.59) * mm, v(27.71, 12.15) * mm, v(27.67, 11.96) * mm, v(27.87, 12) * mm, v(28.64, 12.16) * mm, v(29.4, 12.28) * mm, v(30.16, 12.32) * mm, v(30.45, 12.28) * mm, v(30.64, 12.12) * mm, v(30.64, 11.96) * mm, v(30.4, 11.82) * mm, v(29.46, 11.53) * mm, v(28.37, 11.29) * mm, v(27.51, 11.14) * mm, v(27.32, 11.05) * mm, v(27.05, 10.32) * mm, v(26.8, 9.62) * mm, v(26.76, 9.48) * mm, v(26.8, 9.41) * mm, v(27.3, 9.53) * mm, v(28.09, 9.7) * mm, v(28.55, 9.85) * mm, v(28.76, 9.94) * mm, v(29.03, 9.95) * mm, v(29.35, 9.79) * mm, v(29.88, 9.5) * mm, v(30.24, 9.22) * mm, v(30.26, 9) * mm, v(30.06, 8.8) * mm, v(29.98, 8.66) * mm, v(29.9, 8.03) * mm, v(29.77, 6.35) * mm, v(29.71, 4.62) * mm, v(29.73, 3.8) * mm, v(29.85, 3.78) * mm, v(30.45, 3.84) * mm, v(31.25, 3.93) * mm, v(32.24, 4) * mm, v(32.79, 4.02) * mm, v(33.18, 3.9) * mm, v(33.86, 3.58) * mm, v(34.24, 3.28) * mm, v(34.28, 3.15) * mm, v(34.18, 3.03) * mm, v(33.78, 2.97) * mm, v(32.9, 3.03) * mm, v(31.94, 3.1) * mm, v(30.3, 3.05) * mm, v(28.62, 2.96) * mm, v(27.27, 2.85) * mm, v(25.35, 2.68) * mm, v(23.8, 2.47) * mm, v(22.2, 2.2) * mm], "startDerivative": vector(-3.75, 21.19) * mm, "endDerivative": vector(-65.36, -11.88) * mm});
            skFitSpline(sketch, "E38", {"points": [v(25.14, 3.86) * mm, v(25.13, 4.42) * mm, v(25.18, 4.48) * mm, v(25.79, 4.51) * mm, v(26.89, 4.6) * mm, v(27.74, 4.73) * mm, v(28.09, 4.91) * mm, v(28.13, 5.04) * mm, v(28.03, 5.14) * mm, v(27.63, 5.27) * mm, v(26.85, 5.26) * mm, v(26.02, 5.1) * mm, v(25.25, 5) * mm, v(25.14, 5.04) * mm, v(25.13, 5.83) * mm, v(25.14, 5.95) * mm, v(25.26, 6) * mm, v(25.96, 6.05) * mm, v(27.07, 6.18) * mm, v(27.84, 6.25) * mm, v(27.98, 6.3) * mm, v(28.01, 6.45) * mm, v(27.8, 6.68) * mm, v(27.54, 6.76) * mm, v(26.68, 6.71) * mm, v(25.78, 6.58) * mm, v(25.25, 6.48) * mm, v(25.13, 6.5) * mm, v(25.12, 6.92) * mm, v(25.15, 7.33) * mm, v(25.27, 7.41) * mm, v(25.87, 7.44) * mm, v(26.76, 7.48) * mm, v(27.5, 7.55) * mm, v(27.97, 7.67) * mm, v(28.01, 7.8) * mm, v(27.84, 7.98) * mm, v(27.46, 8.13) * mm, v(26.77, 8.14) * mm, v(26.06, 8) * mm, v(25.3, 7.91) * mm, v(25.17, 7.93) * mm, v(25.12, 8.12) * mm, v(25.13, 8.57) * mm, v(25.15, 8.7) * mm, v(25.37, 8.76) * mm, v(26.23, 8.9) * mm, v(27.1, 9.06) * mm, v(27.87, 9.19) * mm, v(28.32, 9.25) * mm, v(28.6, 9.24) * mm, v(28.84, 9.06) * mm, v(28.92, 8.6) * mm, v(28.91, 7.2) * mm, v(28.93, 4.64) * mm, v(28.91, 3.75) * mm, v(28.85, 3.68) * mm, v(28.03, 3.61) * mm, v(26.85, 3.47) * mm, v(25.71, 3.38) * mm, v(25.23, 3.32) * mm, v(25.14, 3.37) * mm, v(25.14, 3.86) * mm]});
            skFitSpline(sketch, "E39", {"points": [v(23.36, 0.12) * mm, v(24.28, 1) * mm, v(24.86, 1.78) * mm, v(24.97, 2) * mm, v(24.92, 2.2) * mm, v(24.88, 2.34) * mm, v(24.98, 2.46) * mm, v(25.2, 2.49) * mm, v(25.65, 2.4) * mm, v(26.08, 2.2) * mm, v(26.22, 1.87) * mm, v(26.14, 1.6) * mm, v(25.5, 0.9) * mm, v(24.23, -0.1) * mm, v(23.15, -0.73) * mm, v(22.2, -1.14) * mm, v(21.8, -1.27) * mm, v(21.64, -1.21) * mm, v(21.75, -1.1) * mm, v(22.29, -0.72) * mm, v(23.08, -0.14) * mm, v(23.36, 0.12) * mm]});
            skFitSpline(sketch, "E40", {"points": [v(29.04, 0.99) * mm, v(29.65, 0.14) * mm, v(30.42, -0.91) * mm, v(30.58, -1.01) * mm, v(30.76, -0.93) * mm, v(30.87, -0.7) * mm, v(30.87, 0) * mm, v(30.8, 0.38) * mm, v(30.47, 0.99) * mm, v(29.67, 1.77) * mm, v(28.96, 2.23) * mm, v(28.4, 2.37) * mm, v(28.27, 2.33) * mm, v(28.26, 2.2) * mm, v(28.54, 1.8) * mm, v(29.04, 0.99) * mm]});
            skFitSpline(sketch, "E41", {"points": [v(40.24, 3.21) * mm, v(38.7, 2.84) * mm, v(38.31, 2.8) * mm, v(37.9, 3.02) * mm, v(37.44, 3.38) * mm, v(37.42, 3.48) * mm, v(37.64, 3.53) * mm, v(38.82, 3.73) * mm, v(40.06, 3.96) * mm, v(41.44, 4.22) * mm, v(43, 4.51) * mm, v(43.16, 4.51) * mm, v(43.3, 4.95) * mm, v(43.55, 6.3) * mm, v(43.66, 7.32) * mm, v(43.68, 8.48) * mm, v(43.64, 8.87) * mm, v(43.48, 9.16) * mm, v(43.4, 9.31) * mm, v(43.45, 9.5) * mm, v(43.68, 9.54) * mm, v(44.06, 9.44) * mm, v(44.51, 9.24) * mm, v(44.7, 9) * mm, v(44.7, 8.18) * mm, v(44.58, 7.27) * mm, v(44.37, 6.15) * mm, v(44.17, 5.12) * mm, v(44.12, 4.8) * mm, v(44.16, 4.74) * mm, v(44.62, 4.83) * mm, v(45.36, 5) * mm, v(45.91, 5.11) * mm, v(46.65, 5.25) * mm, v(47.42, 5.39) * mm, v(48.1, 5.47) * mm, v(48.54, 5.43) * mm, v(49.1, 5.1) * mm, v(49.45, 4.78) * mm, v(49.5, 4.59) * mm, v(49.3, 4.51) * mm, v(48.43, 4.47) * mm, v(46.97, 4.45) * mm, v(45.74, 4.37) * mm, v(44.5, 4.13) * mm, v(43.93, 4.03) * mm, v(43.8, 3.72) * mm, v(43.3, 2.57) * mm, v(42.63, 1.61) * mm, v(41.77, 0.78) * mm, v(40.56, -0.05) * mm, v(39.21, -0.65) * mm, v(38, -1.05) * mm, v(37.6, -1.11) * mm, v(37.56, -1.06) * mm, v(37.66, -0.95) * mm, v(38.12, -0.68) * mm, v(39.11, -0.21) * mm, v(40.02, 0.35) * mm, v(40.97, 1.05) * mm, v(41.62, 1.63) * mm, v(42.27, 2.43) * mm, v(42.66, 3.17) * mm, v(42.92, 3.73) * mm, v(42.92, 3.78) * mm, v(42.8, 3.8) * mm, v(42.16, 3.67) * mm, v(40.85, 3.38) * mm, v(40.24, 3.21) * mm]});
            skFitSpline(sketch, "E42", {"points": [v(39.35, 9.3) * mm, v(39.2, 8.57) * mm, v(38.85, 7.81) * mm, v(38.46, 7.37) * mm, v(38.32, 7.32) * mm, v(38.21, 7.38) * mm, v(37.96, 7.82) * mm, v(37.84, 8.06) * mm, v(37.87, 8.24) * mm, v(37.97, 8.49) * mm, v(38.18, 8.83) * mm, v(38.37, 9.27) * mm, v(38.66, 10.18) * mm, v(38.82, 10.73) * mm, v(38.87, 10.92) * mm, v(38.95, 10.92) * mm, v(39.2, 10.56) * mm, v(39.27, 10.38) * mm, v(39.5, 10.36) * mm, v(40.27, 10.42) * mm, v(41.66, 10.6) * mm, v(43.2, 10.81) * mm, v(45.36, 11.17) * mm, v(46.29, 11.29) * mm, v(46.7, 11.42) * mm, v(46.87, 11.54) * mm, v(47.21, 11.56) * mm, v(47.5, 11.44) * mm, v(48.32, 10.96) * mm, v(49.05, 10.45) * mm, v(49.1, 10.31) * mm, v(49, 10.18) * mm, v(48.68, 10.08) * mm, v(48.19, 10.04) * mm, v(47.84, 9.88) * mm, v(46.87, 9.1) * mm, v(46.46, 8.81) * mm, v(46.38, 8.81) * mm, v(46.36, 8.9) * mm, v(46.44, 9.3) * mm, v(46.67, 9.93) * mm, v(46.8, 10.34) * mm, v(46.8, 10.52) * mm, v(46.66, 10.63) * mm, v(45.83, 10.58) * mm, v(44.13, 10.4) * mm, v(42.77, 10.2) * mm, v(40.67, 9.94) * mm, v(39.64, 9.83) * mm, v(39.39, 9.78) * mm, v(39.35, 9.75) * mm, v(39.35, 9.3) * mm]});
            skFitSpline(sketch, "E43", {"points": [v(43.21, 11.9) * mm, v(43.62, 11.67) * mm, v(44.03, 11.66) * mm, v(44.19, 11.76) * mm, v(44.2, 12.3) * mm, v(43.77, 12.88) * mm, v(43.13, 13.24) * mm, v(42.28, 13.32) * mm, v(41.88, 13.26) * mm, v(41.85, 13.13) * mm, v(41.93, 12.97) * mm, v(42.3, 12.62) * mm, v(43.03, 12.05) * mm, v(43.21, 11.9) * mm]});
            skFitSpline(sketch, "E44", {"points": [v(40.97, 7.8) * mm, v(41.62, 7.32) * mm, v(42.07, 7.03) * mm, v(42.34, 7.01) * mm, v(42.53, 7.15) * mm, v(42.55, 7.6) * mm, v(42.27, 7.96) * mm, v(41.79, 8.19) * mm, v(41.22, 8.23) * mm, v(40.77, 8.18) * mm, v(40.7, 8.13) * mm, v(40.72, 8.08) * mm, v(40.83, 7.95) * mm, v(40.97, 7.8) * mm]});
            skFitSpline(sketch, "E45", {"points": [v(39.92, 6) * mm, v(40.64, 5.56) * mm, v(41.21, 5.19) * mm, v(41.55, 5.07) * mm, v(41.65, 5.13) * mm, v(41.7, 5.35) * mm, v(41.68, 5.75) * mm, v(41.4, 6.05) * mm, v(40.86, 6.3) * mm, v(40.35, 6.35) * mm, v(39.87, 6.3) * mm, v(39.7, 6.15) * mm, v(39.8, 6.08) * mm, v(39.92, 6) * mm]});
            skFitSpline(sketch, "E46", {"points": [v(45.08, 2.2) * mm, v(44.61, 2.71) * mm, v(44.43, 2.91) * mm, v(44.44, 2.98) * mm, v(44.62, 2.98) * mm, v(46, 2.4) * mm, v(47.02, 1.7) * mm, v(47.72, 0.97) * mm, v(48.08, 0.4) * mm, v(48.19, 0.14) * mm, v(48.19, -0.47) * mm, v(48.07, -0.67) * mm, v(47.88, -0.72) * mm, v(47.4, -0.3) * mm, v(46.6, 0.55) * mm, v(45.86, 1.36) * mm, v(45.33, 1.93) * mm, v(45.08, 2.2) * mm]});
            skSolve(sketch);
        }
        {
            var Q0;
            Q0 = qSketchRegion(id + "F15", true);
            extrude(context, id + "F16", {"entities" : qUnion([Q0]), "operationType" : NewBodyOperationType.ADD, "depth" : 0.5 * mm, "offsetDistance" : 25.4 * mm});
        }
    });
